# Revit family: Wood_Lockers-Salsbury_Industries-32000_Series-1_Wide_Units
name_source: partatom
category: Specialty Equipment
revit_build: Autodesk Revit 2016 (Build: 20150714_1515(x64)
units: mm (PartAtom-declared; Revit-internal decimal feet)

## family parameters
Always vertical = Yes
Cut with Voids When Loaded = No
OmniClass Number = 23.40.00.00
OmniClass Title = Equipment and Furnishings
Part Type = Normal
Room Calculation Point = No
Round Connector Dimension = Use Diameter
Shared = No
Work Plane-Based = No

## types (12) — shared parameters
Assembly Code = C1030310
Door Trim = Rubber Trim - Salsbury Finish - Textured
Hardware = Aluminum - Salsbury Finish - Black Satin
Manufacturer = Salsbury Industries
MasterFormat Code = 10 51 23
MasterFormat Title = Lockers
OmniClass 23 Number = 23.40.00.00
OmniClass 23 Title = Equipment and Furnishings
Primary Structure Materials = Particle Board Industrial Grade - Salsbury Finish - White Melamine Inlay
Secondary Structure Materials = Particle Board Industrial Grade - Salsbury Finish - Black Melamine Overlay
Type Comments = Designer Wood Lockers - Double Tier
URL = www.lockers.com
Unit Trim = Melamine - Salsbury Finish - Black
Width = 12.000"

## per-type parameters (varying)
| type | Base | Base Height | Depth | Description | Door Location D1 | Individual Door Height | Model | Sloping Hood Height | Unit Height | Version |
| 32165 | Wood Locker Bases : Base - 12" W x 15" D Lockers | 4.000" | 15.000" | 1 Wide - 6 Feet High - 15 inches Deep - with Base | Wood Locker Doors : Double Tier Door for Six Foot High Locker | 35.781" | 32165 | 5.743" | 72.000" | 2.0 (07/14/17) |
| 32165 - without Base | Wood Locker Bases : None | 0.000" | 15.000" | 1 Wide - 6 Feet High - 15 inches Deep - without Base | Wood Locker Doors : Double Tier Door for Six Foot High Locker | 35.781" | 32165 without Base | 5.743" | 72.000" | 2.0  (07/14/17) |
| 32168 | Wood Locker Bases : Base - 12" W x 18" D Lockers | 4.000" | 18.000" | 1 Wide - 6 Feet High - 18 inches Deep - with Base | Wood Locker Doors : Double Tier Door for Six Foot High Locker | 35.781" | 32168 | 6.868" | 72.000" | 2.0 (07/14/17) |
| 32168 - without Base | Wood Locker Bases : None | 0.000" | 18.000" | 1 Wide - 6 Feet High - 18 inches Deep - without Base | Wood Locker Doors : Double Tier Door for Six Foot High Locker | 35.781" | 32168 without Base | 6.868" | 72.000" | 2.0 (07/14/17) |
| 32161 | Wood Locker Bases : Base - 12" W x 21" D Lockers | 4.000" | 21.000" | 1 Wide - 6 Feet High - 21 inches Deep - with Base | Wood Locker Doors : Double Tier Door for Six Foot High Locker | 35.781" | 32161 | 7.993" | 72.000" | 2.0 (07/14/17) |
| 32161 - without Base | Wood Locker Bases : None | 0.000" | 21.000" | 1 Wide - 6 Feet High - 21 inches Deep - without Base | Wood Locker Doors : Double Tier Door for Six Foot High Locker | 35.781" | 32161 without Base | 7.993" | 72.000" | 2.0 (07/14/17) |
| 32155 | Wood Locker Bases : Base - 12" W x 15" D Lockers | 4.000" | 15.000" | 1 Wide - 5 Feet High - 15 inches Deep - with Base | Wood Locker Doors : Double Tier Door for Five Foot High Locker | 29.781" | 32155 | 5.743" | 60.000" | 2.0 (07/14/17) |
| 32155 - without Base | Wood Locker Bases : None | 0.000" | 15.000" | 1 Wide - 5 Feet High - 15 inches Deep - without Base | Wood Locker Doors : Double Tier Door for Five Foot High Locker | 29.781" | 32155 without Base | 5.743" | 60.000" | 2.0 (07/14/17) |
| 32158 | Wood Locker Bases : Base - 12" W x 18" D Lockers | 4.000" | 18.000" | 1 Wide - 5 Feet High - 18 inches Deep - with Base | Wood Locker Doors : Double Tier Door for Five Foot High Locker | 29.781" | 32158 | 6.868" | 60.000" | 2.0 (07/14/17) |
| 32158 - without Base | Wood Locker Bases : None | 0.000" | 18.000" | 1 Wide - 5 Feet High - 18 inches Deep - without Base | Wood Locker Doors : Double Tier Door for Five Foot High Locker | 29.781" | 32158 without Base | 6.868" | 60.000" | 2.0 (07/14/17) |
| 32151 | Wood Locker Bases : Base - 12" W x 21" D Lockers | 4.000" | 21.000" | 1 Wide - 5 Feet High - 21 inches Deep - with Base | Wood Locker Doors : Double Tier Door for Five Foot High Locker | 29.781" | 32151 | 7.993" | 60.000" | 2.0 (07/14/17) |
| 32151 - without Base | Wood Locker Bases : None | 0.000" | 21.000" | 1 Wide - 5 Feet High - 21 inches Deep - without Base | Wood Locker Doors : Double Tier Door for Five Foot High Locker | 29.781" | 32151 without Base | 7.993" | 60.000" | 2.0 (07/14/17) |

## geometry (parser evidence)
native form markers: Sweep x28
no freeform markers — native parametric forms only
